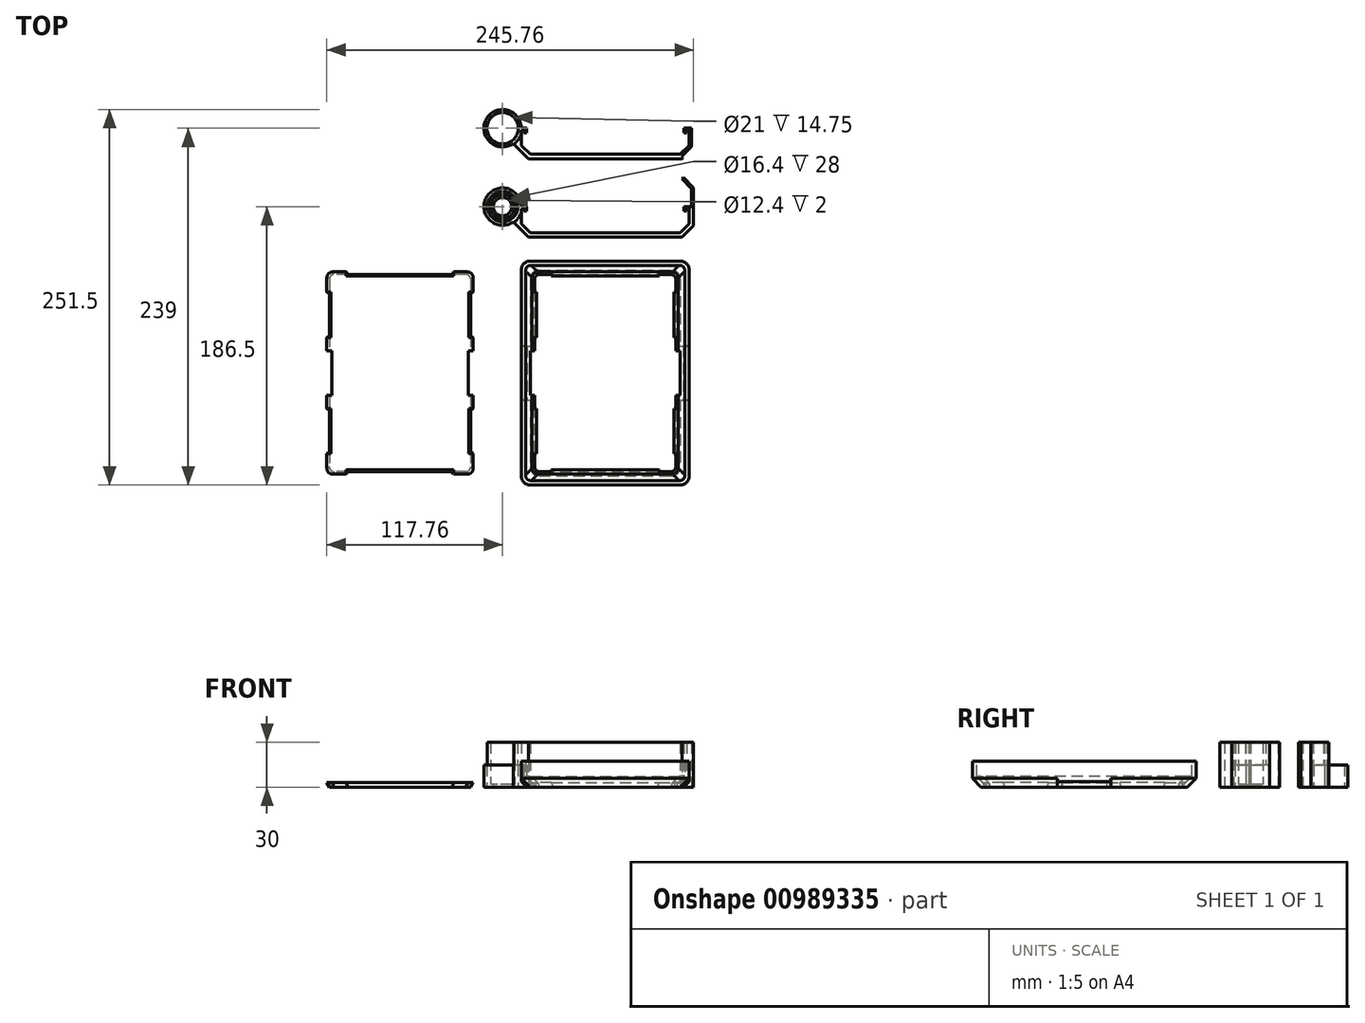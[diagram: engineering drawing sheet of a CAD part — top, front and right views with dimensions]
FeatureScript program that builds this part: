
annotation { "Feature Type Name" : "Feature", "Feature Type Description" : "" }
export const myFeature = defineFeature(function(context is Context, id is Id, definition is map)
    precondition{}
    {
        {
            assignVariable(context, id + "F0", {"name" : "hingeWidth", "anyValue" : 30});
        }
        {
            assignVariable(context, id + "F1", {"name" : "thickness", "anyValue" : 3});
        }
        {
            assignVariable(context, id + "F2", {"name" : "depth", "anyValue" : 17.5});
        }
        {
            var Q0;
            Q0=qCreatedBy(makeId("Top.planeOp"),FACE);
            var sketch = newSketch(context, id + "F3", { "sketchPlane" : qUnion([Q0])});
            skArc(sketch, "E0", {"start": v(12.5, 0) * mm, "mid": v(-11.06, 5.83) * mm, "end": v(7.07, -10.31) * mm});
            skLineSegment(sketch, "E1", {"start": v(0, 0) * mm, "end": v(125, 0) * mm, "construction": true});
            skLineSegment(sketch, "E2", {"start": v(125, -1.25) * mm, "end": v(125, -11.5) * mm});
            skLineSegment(sketch, "E3", {"start": v(125, -11.5) * mm, "end": v(119, -17.5) * mm});
            skLineSegment(sketch, "E4", {"start": v(18.5, -17.5) * mm, "end": v(12.5, -11.5) * mm});
            skLineSegment(sketch, "E5.0", {"start": v(17.26, -20.5) * mm, "end": v(7.07, -10.31) * mm});
            skLineSegment(sketch, "E5.1", {"start": v(120.24, -20.5) * mm, "end": v(17.26, -20.5) * mm});
            skLineSegment(sketch, "E5.2", {"start": v(128, -12.74) * mm, "end": v(120.24, -20.5) * mm});
            skLineSegment(sketch, "E5.3", {"start": v(128, 12.74) * mm, "end": v(128, -12.74) * mm});
            skLineSegment(sketch, "E6", {"start": v(126.5, 12.12) * mm, "end": v(120.14, 18.49) * mm});
            skLineSegment(sketch, "E7", {"start": v(120.14, 18.49) * mm, "end": v(121.2, 19.55) * mm});
            skLineSegment(sketch, "E8", {"start": v(121.2, 19.55) * mm, "end": v(128, 12.74) * mm});
            skLineSegment(sketch, "E9", {"start": v(125, 0) * mm, "end": v(126.5, 0) * mm});
            skLineSegment(sketch, "E10", {"start": v(126.5, 0) * mm, "end": v(126.5, 12.12) * mm});
            skArc(sketch, "E11", {"start": v(7.07, -10.31) * mm, "mid": v(11.06, -5.83) * mm, "end": v(12.5, 0) * mm});
            skArc(sketch, "E12", {"start": v(7.43, -10.67) * mm, "mid": v(10.58, -7.56) * mm, "end": v(12.5, -3.57) * mm});
            skCircle(sketch, "E13", {"center": v(0, 52.5) * mm, "radius": 12.5 * mm});
            skLineSegment(sketch, "E14", {"start": v(7.07, 42.19) * mm, "end": v(17.26, 32) * mm});
            skLineSegment(sketch, "E15", {"start": v(17.26, 32) * mm, "end": v(120.24, 32) * mm});
            skLineSegment(sketch, "E16", {"start": v(120.24, 32) * mm, "end": v(120.84, 32.6) * mm});
            skLineSegment(sketch, "E17", {"start": v(128, 39.76) * mm, "end": v(128, 52.5) * mm, "construction": true});
            skLineSegment(sketch, "E18", {"start": v(128, 52.5) * mm, "end": v(126.5, 52.5) * mm, "construction": true});
            skLineSegment(sketch, "E19", {"start": v(125, 51.25) * mm, "end": v(125, 41) * mm});
            skLineSegment(sketch, "E20", {"start": v(125, 41) * mm, "end": v(119, 35) * mm});
            skLineSegment(sketch, "E21", {"start": v(18.5, 35) * mm, "end": v(12.5, 41) * mm});
            skLineSegment(sketch, "E22", {"start": v(12.5, 41) * mm, "end": v(12.5, 48.93) * mm});
            skArc(sketch, "E23", {"start": v(7.43, 41.83) * mm, "mid": v(10.58, 44.94) * mm, "end": v(12.5, 48.93) * mm});
            skLineSegment(sketch, "E24", {"start": v(126.5, 52.5) * mm, "end": v(126.5, 40.38) * mm});
            skLineSegment(sketch, "E25", {"start": v(126.5, 40.38) * mm, "end": v(119.78, 33.66) * mm});
            skLineSegment(sketch, "E26", {"start": v(119.78, 33.66) * mm, "end": v(120.84, 32.6) * mm});
            skLineSegment(sketch, "E27", {"start": v(120.84, 32.6) * mm, "end": v(128, 39.76) * mm, "construction": true});
            skCircle(sketch, "E28", {"center": v(0, 0) * mm, "radius": 8.2 * mm});
            skCircle(sketch, "E29", {"center": v(0, 52.5) * mm, "radius": 10.5 * mm});
            skCircle(sketch, "E30", {"center": v(0, 0) * mm, "radius": 10.2 * mm});
            skLineSegment(sketch, "E31", {"start": v(12.5, -3.57) * mm, "end": v(12.5, -1.25) * mm});
            skLineSegment(sketch, "E32", {"start": v(125, 52.5) * mm, "end": v(126.5, 52.5) * mm});
            skLineSegment(sketch, "E33", {"start": v(12.5, 52.5) * mm, "end": v(125, 52.5) * mm, "construction": true});
            skCircle(sketch, "E34", {"center": v(0, 0) * mm, "radius": 6.2 * mm});
            skLineSegment(sketch, "E35", {"start": v(12.5, -3.57) * mm, "end": v(12.5, -11.5) * mm});
            skLineSegment(sketch, "E36", {"start": v(125, 52.5) * mm, "end": v(121.5, 52.5) * mm});
            skLineSegment(sketch, "E37", {"start": v(121.5, 52.5) * mm, "end": v(121.5, 49.5) * mm});
            skLineSegment(sketch, "E38", {"start": v(121.5, 49.5) * mm, "end": v(123.25, 49.5) * mm});
            skLineSegment(sketch, "E39", {"start": v(123.25, 49.5) * mm, "end": v(123.25, 51.25) * mm});
            skLineSegment(sketch, "E40", {"start": v(123.25, 51.25) * mm, "end": v(125, 51.25) * mm});
            skLineSegment(sketch, "E41", {"start": v(12.5, 52.5) * mm, "end": v(16, 52.5) * mm});
            skLineSegment(sketch, "E42", {"start": v(16, 52.5) * mm, "end": v(16, 49.5) * mm});
            skLineSegment(sketch, "E43", {"start": v(16, 49.5) * mm, "end": v(14.25, 49.5) * mm});
            skLineSegment(sketch, "E44", {"start": v(14.25, 49.5) * mm, "end": v(14.25, 51.25) * mm});
            skLineSegment(sketch, "E45", {"start": v(14.25, 51.25) * mm, "end": v(12.5, 51.25) * mm});
            skLineSegment(sketch, "E46", {"start": v(125, 0) * mm, "end": v(121.5, 0) * mm});
            skLineSegment(sketch, "E47", {"start": v(121.5, 0) * mm, "end": v(121.5, -3) * mm});
            skLineSegment(sketch, "E48", {"start": v(121.5, -3) * mm, "end": v(123.25, -3) * mm});
            skLineSegment(sketch, "E49", {"start": v(123.25, -3) * mm, "end": v(123.25, -1.25) * mm});
            skLineSegment(sketch, "E50", {"start": v(123.25, -1.25) * mm, "end": v(125, -1.25) * mm});
            skLineSegment(sketch, "E51", {"start": v(12.5, 0) * mm, "end": v(16, 0) * mm});
            skLineSegment(sketch, "E52", {"start": v(16, 0) * mm, "end": v(16, -3) * mm});
            skLineSegment(sketch, "E53", {"start": v(16, -3) * mm, "end": v(14.25, -3) * mm});
            skLineSegment(sketch, "E54", {"start": v(14.25, -3) * mm, "end": v(14.25, -1.25) * mm});
            skLineSegment(sketch, "E55", {"start": v(14.25, -1.25) * mm, "end": v(12.5, -1.25) * mm});
            skPoint(sketch, "E55.endSnap0", {"position": v(12.5, -1.79) * mm});
            skLineSegment(sketch, "E56", {"start": v(18.5, 35) * mm, "end": v(119, 35) * mm});
            skLineSegment(sketch, "E57", {"start": v(18.5, -17.5) * mm, "end": v(119, -17.5) * mm});
            skLineSegment(sketch, "E58", {"start": v(12.5, 48.93) * mm, "end": v(12.5, 51.25) * mm});
            skSolve(sketch);
        }
        {
            var Q0;
            {var subQ3=sQuery(id+"F3.wireOp",EDGE,"E15");Q0=makeQuery(id+"F3.imprint","IMPRINT",FACE,{"disambiguationData":[TD([[makeQuery(id+"F3.imprint","IMPRINT",EDGE,{"derivedFrom":subQ3}),1.0]])]});}
            var Q1;
            Q1=makeQuery(id+"F3.imprint","IMPRINT",FACE,{"disambiguationData":[TD([[makeQuery(id+"F3.imprint","IMPRINT",EDGE,{"derivedFrom":sQuery(id+"F3.wireOp",EDGE,"E2")}),1.0]])]});
            var Q2;
            Q2=makeQuery(id+"F3.imprint","IMPRINT",FACE,{"disambiguationData":[TD([[makeQuery(id+"F3.imprint","IMPRINT",EDGE,{"derivedFrom":sQuery(id+"F3.wireOp",EDGE,"E28")}),-1.0]])]});
            extrude(context, id + "F4", {"entities" : qUnion([Q0, Q1, Q2]), "depth" : (getVariable(context, 'hingeWidth')) * mm, "offsetDistance" : 25 * mm});
        }
        {
            var Q0;
            Q0=makeQuery(id+"F3.imprint","IMPRINT",FACE,{"disambiguationData":[TD([[makeQuery(id+"F3.imprint","IMPRINT",EDGE,{"derivedFrom":sQuery(id+"F3.wireOp",EDGE,"E29")}),-1.0]])]});
            var Q1;
            {var subQ5=sQuery(id+"F3.wireOp",EDGE,"E23");Q1=makeQuery(id+"F3.imprint","IMPRINT",FACE,{"disambiguationData":[TD([[makeQuery(id+"F3.imprint","IMPRINT",EDGE,{"derivedFrom":subQ5}),1.0]])]});}
            var Q2;
            Q2=makeQuery(id+"F3.imprint","IMPRINT",FACE,{"disambiguationData":[TD([[makeQuery(id+"F3.imprint","IMPRINT",EDGE,{"derivedFrom":sQuery(id+"F3.wireOp",EDGE,"E0")}),1.0]])]});
            var Q3;
            Q3=makeQuery(id+"F3.imprint","IMPRINT",FACE,{"disambiguationData":[TD([[makeQuery(id+"F3.imprint","IMPRINT",EDGE,{"derivedFrom":sQuery(id+"F3.wireOp",EDGE,"E28")}),-1.0]])]});
            var Q4;
            {var subQ0=sQuery(id+"F3.wireOp",EDGE,"E11");Q4=makeQuery(id+"F3.imprint","IMPRINT",FACE,{"disambiguationData":[TD([[makeQuery(id+"F3.imprint","IMPRINT",EDGE,{"derivedFrom":subQ0}),-1.0]])]});}
            extrude(context, id + "F5", {"entities" : qUnion([Q0, Q1, Q2, Q3, Q4]), "operationType" : NewBodyOperationType.ADD, "depth" : ((getVariable(context, 'hingeWidth') / 2) - .25) * mm, "offsetDistance" : 25 * mm});
        }
        {
            var Q0;
            Q0=makeQuery(id+"F3.imprint","IMPRINT",FACE,{"disambiguationData":[TD([[makeQuery(id+"F3.imprint","IMPRINT",EDGE,{"derivedFrom":sQuery(id+"F3.wireOp",EDGE,"E28")}),1.0]])]});
            extrude(context, id + "F6", {"entities" : qUnion([Q0]), "operationType" : NewBodyOperationType.ADD, "depth" : 2 * mm, "offsetDistance" : 25 * mm});
        }
        {
            var Q0;
            Q0=qCreatedBy(makeId("Top.planeOp"),FACE);
            var sketch = newSketch(context, id + "F7", { "sketchPlane" : qUnion([Q0])});
            skLineSegment(sketch, "E59.0", {"start": v(18.5, -17.5) * mm, "end": v(12.5, -11.5) * mm, "construction": true});
            skLineSegment(sketch, "E60.0", {"start": v(119, -17.5) * mm, "end": v(18.5, -17.5) * mm, "construction": true});
            skLineSegment(sketch, "E61.0", {"start": v(125, -11.5) * mm, "end": v(119, -17.5) * mm, "construction": true});
            skLineSegment(sketch, "E62", {"start": v(12.5, -11.5) * mm, "end": v(12.5, -36.5) * mm, "construction": true});
            skLineSegment(sketch, "E63", {"start": v(12.5, -36.5) * mm, "end": v(18.5, -36.5) * mm, "construction": true});
            skLineSegment(sketch, "E64", {"start": v(18.5, -36.5) * mm, "end": v(119, -36.5) * mm, "construction": true});
            skLineSegment(sketch, "E65", {"start": v(119, -36.5) * mm, "end": v(125, -36.5) * mm, "construction": true});
            skLineSegment(sketch, "E66", {"start": v(125, -36.5) * mm, "end": v(125, -42.5) * mm, "construction": true});
            skLineSegment(sketch, "E67", {"start": v(12.5, -36.5) * mm, "end": v(12.5, -42.5) * mm, "construction": true});
            skLineSegment(sketch, "E68", {"start": v(12.5, -42.5) * mm, "end": v(12.5, -180.5) * mm, "construction": true});
            skLineSegment(sketch, "E69", {"start": v(12.5, -180.5) * mm, "end": v(12.5, -186.5) * mm, "construction": true});
            skLineSegment(sketch, "E70", {"start": v(12.5, -186.5) * mm, "end": v(18.5, -186.5) * mm, "construction": true});
            skLineSegment(sketch, "E71", {"start": v(18.5, -186.5) * mm, "end": v(119, -186.5) * mm, "construction": true});
            skLineSegment(sketch, "E72", {"start": v(119, -186.5) * mm, "end": v(125, -186.5) * mm, "construction": true});
            skLineSegment(sketch, "E73", {"start": v(125, -186.5) * mm, "end": v(125, -180.5) * mm, "construction": true});
            skLineSegment(sketch, "E74", {"start": v(125, -180.5) * mm, "end": v(125, -42.5) * mm, "construction": true});
            skLineSegment(sketch, "E75.bottom", {"start": v(24.5, -42.5) * mm, "end": v(113, -42.5) * mm});
            skLineSegment(sketch, "E75.top", {"start": v(24.5, -180.5) * mm, "end": v(113, -180.5) * mm});
            skLineSegment(sketch, "E75.left", {"start": v(18.5, -48.5) * mm, "end": v(18.5, -174.5) * mm});
            skLineSegment(sketch, "E75.right", {"start": v(119, -48.5) * mm, "end": v(119, -174.5) * mm});
            skPoint(sketch, "E76.visualSharp", {"position": v(18.5, -42.5) * mm});
            skArc(sketch, "E76.filletArc", {"start": v(24.5, -42.5) * mm, "mid": v(20.26, -44.26) * mm, "end": v(18.5, -48.5) * mm});
            skPoint(sketch, "E77.visualSharp", {"position": v(119, -42.5) * mm});
            skArc(sketch, "E77.filletArc", {"start": v(119, -48.5) * mm, "mid": v(117.24, -44.26) * mm, "end": v(113, -42.5) * mm});
            skPoint(sketch, "E78.visualSharp", {"position": v(119, -180.5) * mm});
            skArc(sketch, "E78.filletArc", {"start": v(113, -180.5) * mm, "mid": v(117.24, -178.74) * mm, "end": v(119, -174.5) * mm});
            skPoint(sketch, "E79.visualSharp", {"position": v(18.5, -180.5) * mm});
            skArc(sketch, "E79.filletArc", {"start": v(18.5, -174.5) * mm, "mid": v(20.26, -178.74) * mm, "end": v(24.5, -180.5) * mm});
            skLineSegment(sketch, "E80", {"start": v(0, 0) * mm, "end": v(0, -36.5) * mm, "construction": true});
            skArc(sketch, "E81.0", {"start": v(24.5, -45.5) * mm, "mid": v(22.38, -46.38) * mm, "end": v(21.5, -48.5) * mm, "construction": true});
            skLineSegment(sketch, "E81.1", {"start": v(21.5, -48.5) * mm, "end": v(21.5, -174.5) * mm, "construction": true});
            skLineSegment(sketch, "E81.2", {"start": v(24.5, -45.5) * mm, "end": v(113, -45.5) * mm, "construction": true});
            skArc(sketch, "E81.3", {"start": v(21.5, -174.5) * mm, "mid": v(22.38, -176.62) * mm, "end": v(24.5, -177.5) * mm, "construction": true});
            skArc(sketch, "E81.4", {"start": v(116, -48.5) * mm, "mid": v(115.12, -46.38) * mm, "end": v(113, -45.5) * mm, "construction": true});
            skLineSegment(sketch, "E81.5", {"start": v(116, -48.5) * mm, "end": v(116, -174.5) * mm, "construction": true});
            skArc(sketch, "E81.6", {"start": v(113, -177.5) * mm, "mid": v(115.12, -176.62) * mm, "end": v(116, -174.5) * mm, "construction": true});
            skLineSegment(sketch, "E81.7", {"start": v(24.5, -177.5) * mm, "end": v(113, -177.5) * mm, "construction": true});
            skLineSegment(sketch, "E82.MirrorCS", {"start": v(-21.5, -48.5) * mm, "end": v(-21.5, -174.5) * mm});
            skArc(sketch, "E83.MirrorCS", {"start": v(-24.5, -45.5) * mm, "mid": v(-22.38, -46.38) * mm, "end": v(-21.5, -48.5) * mm});
            skLineSegment(sketch, "E84.MirrorCS", {"start": v(-24.5, -45.5) * mm, "end": v(-113, -45.5) * mm});
            skArc(sketch, "E85.MirrorCS", {"start": v(-116, -48.5) * mm, "mid": v(-115.12, -46.38) * mm, "end": v(-113, -45.5) * mm});
            skLineSegment(sketch, "E86.MirrorCS", {"start": v(-116, -48.5) * mm, "end": v(-116, -174.5) * mm});
            skArc(sketch, "E87.MirrorCS", {"start": v(-113, -177.5) * mm, "mid": v(-115.12, -176.62) * mm, "end": v(-116, -174.5) * mm});
            skLineSegment(sketch, "E88.MirrorCS", {"start": v(-24.5, -177.5) * mm, "end": v(-113, -177.5) * mm});
            skArc(sketch, "E89.MirrorCS", {"start": v(-21.5, -174.5) * mm, "mid": v(-22.38, -176.62) * mm, "end": v(-24.5, -177.5) * mm});
            skLineSegment(sketch, "E90", {"start": v(0, -36.5) * mm, "end": v(0, -186.5) * mm, "construction": true});
            skLineSegment(sketch, "E91", {"start": v(0, -111.5) * mm, "end": v(12.5, -111.5) * mm, "construction": true});
            skLineSegment(sketch, "E92", {"start": v(0, -96.5) * mm, "end": v(12.5, -96.5) * mm, "construction": true});
            skLineSegment(sketch, "E93", {"start": v(0, -126.5) * mm, "end": v(12.5, -126.5) * mm, "construction": true});
            skSolve(sketch);
        }
        {
            var Q0;
            Q0=qCreatedBy(makeId("Top.planeOp"),FACE);
            cPlane(context, id + "F8", {"entities" : qUnion([Q0]), "cplaneType" : CPlaneType.OFFSET, "offset" : (getVariable(context, 'thickness') * 2) * mm, "width" : 150 * mm, "height" : 150 * mm});
        }
        {
            var Q0;
            Q0=qCreatedBy(id+"F8.planeOp",FACE);
            var sketch = newSketch(context, id + "F9", { "sketchPlane" : qUnion([Q0])});
            skPoint(sketch, "E94.0", {"position": v(12.5, -36.5) * mm});
            skPoint(sketch, "E95.0", {"position": v(125, -186.5) * mm});
            skLineSegment(sketch, "E96.bottom", {"start": v(18.5, -36.5) * mm, "end": v(119, -36.5) * mm});
            skLineSegment(sketch, "E96.top", {"start": v(18.5, -186.5) * mm, "end": v(119, -186.5) * mm});
            skLineSegment(sketch, "E96.left", {"start": v(12.5, -42.5) * mm, "end": v(12.5, -180.5) * mm});
            skLineSegment(sketch, "E96.right", {"start": v(125, -42.5) * mm, "end": v(125, -180.5) * mm});
            skArc(sketch, "E97.filletArc", {"start": v(18.5, -36.5) * mm, "mid": v(14.26, -38.26) * mm, "end": v(12.5, -42.5) * mm});
            skPoint(sketch, "E98.visualSharp", {"position": v(125, -36.5) * mm});
            skArc(sketch, "E98.filletArc", {"start": v(125, -42.5) * mm, "mid": v(123.24, -38.26) * mm, "end": v(119, -36.5) * mm});
            skArc(sketch, "E99.filletArc", {"start": v(119, -186.5) * mm, "mid": v(123.24, -184.74) * mm, "end": v(125, -180.5) * mm});
            skPoint(sketch, "E100.visualSharp", {"position": v(12.5, -186.5) * mm});
            skArc(sketch, "E100.filletArc", {"start": v(12.5, -180.5) * mm, "mid": v(14.26, -184.74) * mm, "end": v(18.5, -186.5) * mm});
            skSolve(sketch);
        }
        {
            var Q0;
            Q0 = qSketchRegion(id + "F9", true);
            var Q1;
            Q1=makeQuery(id+"F7.imprint","IMPRINT",FACE,{"disambiguationData":[TD([[makeQuery(id+"F7.imprint","IMPRINT",EDGE,{"derivedFrom":sQuery(id+"F7.wireOp",EDGE,"E75.bottom")}),-1.0]])]});
            loft(context, id + "F10", {"sheetProfilesArray" : [{ "sheetProfileEntities" : qUnion([Q0]) }, { "sheetProfileEntities" : qUnion([Q1]) }]});
        }
        {
            var Q0;
            Q0 = qSketchRegion(id + "F9", true);
            extrude(context, id + "F11", {"entities" : qUnion([Q0]), "operationType" : NewBodyOperationType.ADD, "depth" : (getVariable(context, 'depth') - (getVariable(context, 'thickness') * 2)) * mm, "offsetDistance" : 25 * mm});
        }
        {
            var Q0;
            Q0=makeQuery(id+"F11.opExtrude","CAP_FACE",FACE,{"disambiguationData":[OSD([sQuery(id+"F9.wireOp",EDGE,"E96.bottom"),sQuery(id+"F9.wireOp",EDGE,"E96.top"),sQuery(id+"F9.wireOp",EDGE,"E96.left"),sQuery(id+"F9.wireOp",EDGE,"E96.right"),sQuery(id+"F9.wireOp",EDGE,"E97.filletArc"),sQuery(id+"F9.wireOp",EDGE,"E98.filletArc"),sQuery(id+"F9.wireOp",EDGE,"E99.filletArc"),sQuery(id+"F9.wireOp",EDGE,"E100.filletArc")])],"isStart":false});
            shell(context, id + "F12", {"entities" : qUnion([Q0]), "thickness" : (getVariable(context, 'thickness')) * mm});
        }
        {
            var Q0;
            Q0=makeQuery(id+"F12.opShell","OFFSET_FACE",FACE,{"disambiguationData":[OSD([makeQuery(id+"F7.imprint","IMPRINT",FACE,{"disambiguationData":[TD([[makeQuery(id+"F7.imprint","IMPRINT",EDGE,{"derivedFrom":sQuery(id+"F7.wireOp",EDGE,"E75.bottom")}),-1.0]])]})])]});
            var sketch = newSketch(context, id + "F13", { "sketchPlane" : qUnion([Q0])});
            skFitSpline(sketch, "E101.0.0", {"points": [v(19.74, -175.38) * mm, v(19.74, -175.5) * mm, v(19.76, -175.76) * mm, v(19.83, -176.13) * mm, v(19.93, -176.5) * mm, v(20.07, -176.84) * mm, v(20.24, -177.17) * mm, v(20.51, -177.6) * mm, v(20.83, -177.99) * mm, v(21.2, -178.33) * mm, v(21.6, -178.63) * mm, v(22.04, -178.88) * mm, v(22.51, -179.07) * mm, v(23, -179.2) * mm, v(23.37, -179.26) * mm, v(23.62, -179.26) * mm], "construction": true});
            skLineSegment(sketch, "E101.0.1", {"start": v(113.88, -179.26) * mm, "end": v(23.62, -179.26) * mm, "construction": true});
            skFitSpline(sketch, "E101.0.2", {"points": [v(113.88, -179.26) * mm, v(114, -179.26) * mm, v(114.26, -179.24) * mm, v(114.63, -179.17) * mm, v(115, -179.07) * mm, v(115.34, -178.93) * mm, v(115.67, -178.76) * mm, v(116.1, -178.49) * mm, v(116.49, -178.17) * mm, v(116.83, -177.8) * mm, v(117.13, -177.4) * mm, v(117.38, -176.96) * mm, v(117.57, -176.49) * mm, v(117.7, -176) * mm, v(117.76, -175.63) * mm, v(117.76, -175.38) * mm], "construction": true});
            skLineSegment(sketch, "E101.0.3", {"start": v(117.76, -175.38) * mm, "end": v(117.76, -47.62) * mm, "construction": true});
            skFitSpline(sketch, "E101.0.4", {"points": [v(117.76, -47.62) * mm, v(117.76, -47.5) * mm, v(117.74, -47.24) * mm, v(117.67, -46.87) * mm, v(117.57, -46.5) * mm, v(117.43, -46.16) * mm, v(117.26, -45.83) * mm, v(116.99, -45.4) * mm, v(116.67, -45.01) * mm, v(116.3, -44.67) * mm, v(115.9, -44.37) * mm, v(115.46, -44.12) * mm, v(114.99, -43.93) * mm, v(114.5, -43.8) * mm, v(114.13, -43.74) * mm, v(113.88, -43.74) * mm], "construction": true});
            skLineSegment(sketch, "E101.0.5", {"start": v(113.88, -43.74) * mm, "end": v(23.62, -43.74) * mm, "construction": true});
            skFitSpline(sketch, "E101.0.6", {"points": [v(23.62, -43.74) * mm, v(23.5, -43.74) * mm, v(23.24, -43.76) * mm, v(22.87, -43.83) * mm, v(22.5, -43.93) * mm, v(22.16, -44.07) * mm, v(21.83, -44.24) * mm, v(21.4, -44.51) * mm, v(21.01, -44.83) * mm, v(20.67, -45.2) * mm, v(20.37, -45.6) * mm, v(20.12, -46.04) * mm, v(19.93, -46.51) * mm, v(19.8, -47) * mm, v(19.74, -47.37) * mm, v(19.74, -47.62) * mm], "construction": true});
            skLineSegment(sketch, "E101.0.7", {"start": v(19.74, -175.38) * mm, "end": v(19.74, -47.62) * mm, "construction": true});
            skLineSegment(sketch, "E102.0", {"start": v(0, 0) * mm, "end": v(0, -36.5) * mm, "construction": true});
            skLineSegment(sketch, "E103.MirrorCS", {"start": v(-113.88, -43.74) * mm, "end": v(-23.62, -43.74) * mm});
            skLineSegment(sketch, "E104.MirrorCS", {"start": v(-19.74, -175.38) * mm, "end": v(-19.74, -47.62) * mm});
            skLineSegment(sketch, "E105.MirrorCS", {"start": v(-113.88, -179.26) * mm, "end": v(-23.62, -179.26) * mm});
            skLineSegment(sketch, "E106.MirrorCS", {"start": v(-117.76, -175.38) * mm, "end": v(-117.76, -47.62) * mm});
            skArc(sketch, "E107", {"start": v(-113.88, -43.74) * mm, "mid": v(-116.62, -44.88) * mm, "end": v(-117.76, -47.62) * mm});
            skArc(sketch, "E108", {"start": v(-19.74, -47.62) * mm, "mid": v(-20.88, -44.88) * mm, "end": v(-23.62, -43.74) * mm});
            skArc(sketch, "E109", {"start": v(-23.62, -179.26) * mm, "mid": v(-20.88, -178.12) * mm, "end": v(-19.74, -175.38) * mm});
            skArc(sketch, "E110", {"start": v(-117.76, -175.38) * mm, "mid": v(-116.62, -178.12) * mm, "end": v(-113.88, -179.26) * mm});
            skSolve(sketch);
        }
        {
            var Q0;
            Q0=makeQuery(id+"F7.imprint","IMPRINT",FACE,{"disambiguationData":[TD([[makeQuery(id+"F7.imprint","IMPRINT",EDGE,{"derivedFrom":sQuery(id+"F7.wireOp",EDGE,"E82.MirrorCS")}),-1.0]])]});
            var Q1;
            Q1=makeQuery(id+"F13.imprint","IMPRINT",FACE,{"disambiguationData":[TD([[makeQuery(id+"F13.imprint","IMPRINT",EDGE,{"derivedFrom":sQuery(id+"F13.wireOp",EDGE,"E103.MirrorCS")}),-1.0]])]});
            loft(context, id + "F14", {"sheetProfilesArray" : [{ "sheetProfileEntities" : qUnion([Q0]) }, { "sheetProfileEntities" : qUnion([Q1]) }]});
        }
        {
            var Q0;
            Q0=qCreatedBy(makeId("Top.planeOp"),FACE);
            var sketch = newSketch(context, id + "F15", { "sketchPlane" : qUnion([Q0])});
            skLineSegment(sketch, "E111.0", {"start": v(-24.5, -45.5) * mm, "end": v(-113, -45.5) * mm, "construction": true});
            skLineSegment(sketch, "E112.0", {"start": v(-116, -48.5) * mm, "end": v(-116, -174.5) * mm, "construction": true});
            skLineSegment(sketch, "E113.0", {"start": v(-21.5, -48.5) * mm, "end": v(-21.5, -174.5) * mm, "construction": true});
            skLineSegment(sketch, "E114.0", {"start": v(-24.5, -177.5) * mm, "end": v(-113, -177.5) * mm, "construction": true});
            skLineSegment(sketch, "E115.0", {"start": v(-23.62, -43.74) * mm, "end": v(-113.88, -43.74) * mm, "construction": true});
            skLineSegment(sketch, "E116.0", {"start": v(-113.88, -179.26) * mm, "end": v(-23.62, -179.26) * mm, "construction": true});
            skLineSegment(sketch, "E117.0", {"start": v(-19.74, -175.38) * mm, "end": v(-19.74, -47.62) * mm, "construction": true});
            skLineSegment(sketch, "E118.0", {"start": v(-117.76, -47.62) * mm, "end": v(-117.76, -175.38) * mm, "construction": true});
            skLineSegment(sketch, "E119.bottom", {"start": v(-103.75, -43.74) * mm, "end": v(-33.75, -43.74) * mm});
            skLineSegment(sketch, "E119.top", {"start": v(-103.75, -45.5) * mm, "end": v(-33.75, -45.5) * mm});
            skLineSegment(sketch, "E119.left", {"start": v(-103.75, -43.74) * mm, "end": v(-103.75, -45.5) * mm});
            skLineSegment(sketch, "E119.right", {"start": v(-33.75, -43.74) * mm, "end": v(-33.75, -45.5) * mm});
            skLineSegment(sketch, "E120", {"start": v(-68.75, -43.74) * mm, "end": v(-68.75, -45.5) * mm, "construction": true});
            skLineSegment(sketch, "E121.bottom", {"start": v(-103.75, -177.5) * mm, "end": v(-33.75, -177.5) * mm});
            skLineSegment(sketch, "E121.top", {"start": v(-103.75, -179.26) * mm, "end": v(-33.75, -179.26) * mm});
            skLineSegment(sketch, "E121.left", {"start": v(-103.75, -177.5) * mm, "end": v(-103.75, -179.26) * mm});
            skLineSegment(sketch, "E121.right", {"start": v(-33.75, -177.5) * mm, "end": v(-33.75, -179.26) * mm});
            skLineSegment(sketch, "E122.0", {"start": v(0, -126.5) * mm, "end": v(12.5, -126.5) * mm, "construction": true});
            skLineSegment(sketch, "E123.0", {"start": v(0, -111.5) * mm, "end": v(12.5, -111.5) * mm, "construction": true});
            skLineSegment(sketch, "E124.0", {"start": v(0, -96.5) * mm, "end": v(12.5, -96.5) * mm, "construction": true});
            skLineSegment(sketch, "E125.bottom", {"start": v(-19.74, -126.5) * mm, "end": v(-23, -126.5) * mm});
            skLineSegment(sketch, "E125.top", {"start": v(-19.74, -96.5) * mm, "end": v(-23, -96.5) * mm});
            skLineSegment(sketch, "E125.left", {"start": v(-19.74, -126.5) * mm, "end": v(-19.74, -96.5) * mm});
            skLineSegment(sketch, "E125.right", {"start": v(-23, -126.5) * mm, "end": v(-23, -96.5) * mm});
            skLineSegment(sketch, "E126.bottom", {"start": v(-114.5, -96.5) * mm, "end": v(-117.76, -96.5) * mm});
            skLineSegment(sketch, "E126.top", {"start": v(-114.5, -126.5) * mm, "end": v(-117.76, -126.5) * mm});
            skLineSegment(sketch, "E126.left", {"start": v(-114.5, -96.5) * mm, "end": v(-114.5, -126.5) * mm});
            skLineSegment(sketch, "E126.right", {"start": v(-117.76, -96.5) * mm, "end": v(-117.76, -126.5) * mm});
            skLineSegment(sketch, "E127.bottom", {"start": v(-19.74, -86.5) * mm, "end": v(-21.5, -86.5) * mm});
            skLineSegment(sketch, "E127.top", {"start": v(-19.74, -58.5) * mm, "end": v(-21.5, -58.5) * mm});
            skLineSegment(sketch, "E127.left", {"start": v(-19.74, -86.5) * mm, "end": v(-19.74, -58.5) * mm});
            skLineSegment(sketch, "E127.right", {"start": v(-21.5, -86.5) * mm, "end": v(-21.5, -58.5) * mm});
            skLineSegment(sketch, "E128.bottom", {"start": v(-21.5, -136.5) * mm, "end": v(-19.74, -136.5) * mm});
            skLineSegment(sketch, "E128.top", {"start": v(-21.5, -164.5) * mm, "end": v(-19.74, -164.5) * mm});
            skLineSegment(sketch, "E128.left", {"start": v(-21.5, -136.5) * mm, "end": v(-21.5, -164.5) * mm});
            skLineSegment(sketch, "E128.right", {"start": v(-19.74, -136.5) * mm, "end": v(-19.74, -164.5) * mm});
            skLineSegment(sketch, "E129.bottom", {"start": v(-116, -58.5) * mm, "end": v(-117.76, -58.5) * mm});
            skLineSegment(sketch, "E129.top", {"start": v(-116, -86.5) * mm, "end": v(-117.76, -86.5) * mm});
            skLineSegment(sketch, "E129.left", {"start": v(-116, -58.5) * mm, "end": v(-116, -86.5) * mm});
            skLineSegment(sketch, "E129.right", {"start": v(-117.76, -58.5) * mm, "end": v(-117.76, -86.5) * mm});
            skLineSegment(sketch, "E130.bottom", {"start": v(-116, -136.5) * mm, "end": v(-117.76, -136.5) * mm});
            skLineSegment(sketch, "E130.top", {"start": v(-116, -164.5) * mm, "end": v(-117.76, -164.5) * mm});
            skLineSegment(sketch, "E130.left", {"start": v(-116, -136.5) * mm, "end": v(-116, -164.5) * mm});
            skLineSegment(sketch, "E130.right", {"start": v(-117.76, -136.5) * mm, "end": v(-117.76, -164.5) * mm});
            skLineSegment(sketch, "E131.0", {"start": v(21.5, -48.5) * mm, "end": v(21.5, -174.5) * mm, "construction": true});
            skLineSegment(sketch, "E132.0", {"start": v(116, -48.5) * mm, "end": v(116, -174.5) * mm, "construction": true});
            skLineSegment(sketch, "E133.bottom", {"start": v(21.5, -96.5) * mm, "end": v(18.5, -96.5) * mm});
            skLineSegment(sketch, "E133.top", {"start": v(21.5, -126.5) * mm, "end": v(18.5, -126.5) * mm});
            skLineSegment(sketch, "E133.left", {"start": v(21.5, -96.5) * mm, "end": v(21.5, -126.5) * mm});
            skLineSegment(sketch, "E134.0", {"start": v(18.5, -48.5) * mm, "end": v(18.5, -174.5) * mm, "construction": true});
            skLineSegment(sketch, "E135.bottom", {"start": v(116, -96.5) * mm, "end": v(119, -96.5) * mm});
            skLineSegment(sketch, "E135.top", {"start": v(116, -126.5) * mm, "end": v(119, -126.5) * mm});
            skLineSegment(sketch, "E135.left", {"start": v(116, -96.5) * mm, "end": v(116, -126.5) * mm});
            skLineSegment(sketch, "E135.right", {"start": v(119, -96.5) * mm, "end": v(119, -126.5) * mm});
            skLineSegment(sketch, "E136.bottom", {"start": v(119, -96.5) * mm, "end": v(119, -96.5) * mm});
            skLineSegment(sketch, "E136.top", {"start": v(119, -126.5) * mm, "end": v(119, -126.5) * mm});
            skLineSegment(sketch, "E137", {"start": v(18.5, -96.5) * mm, "end": v(18.5, -126.5) * mm});
            skSolve(sketch);
        }
        {
            var Q0;
            Q0=makeQuery(id+"F15.imprint","IMPRINT",FACE,{"disambiguationData":[TD([[makeQuery(id+"F15.imprint","IMPRINT",EDGE,{"derivedFrom":sQuery(id+"F15.wireOp",EDGE,"E119.bottom")}),-1.0]])]});
            var Q1;
            Q1=makeQuery(id+"F15.imprint","IMPRINT",FACE,{"disambiguationData":[TD([[makeQuery(id+"F15.imprint","IMPRINT",EDGE,{"derivedFrom":sQuery(id+"F15.wireOp",EDGE,"E121.bottom")}),-1.0]])]});
            var Q2;
            Q2=makeQuery(id+"F15.imprint","IMPRINT",FACE,{"disambiguationData":[TD([[makeQuery(id+"F15.imprint","IMPRINT",EDGE,{"derivedFrom":sQuery(id+"F15.wireOp",EDGE,"E129.bottom")}),1.0]])]});
            var Q3;
            Q3=makeQuery(id+"F15.imprint","IMPRINT",FACE,{"disambiguationData":[TD([[makeQuery(id+"F15.imprint","IMPRINT",EDGE,{"derivedFrom":sQuery(id+"F15.wireOp",EDGE,"E130.bottom")}),1.0]])]});
            var Q4;
            Q4=makeQuery(id+"F15.imprint","IMPRINT",FACE,{"disambiguationData":[TD([[makeQuery(id+"F15.imprint","IMPRINT",EDGE,{"derivedFrom":sQuery(id+"F15.wireOp",EDGE,"E127.bottom")}),-1.0]])]});
            var Q5;
            Q5=makeQuery(id+"F15.imprint","IMPRINT",FACE,{"disambiguationData":[TD([[makeQuery(id+"F15.imprint","IMPRINT",EDGE,{"derivedFrom":sQuery(id+"F15.wireOp",EDGE,"E128.bottom")}),-1.0]])]});
            extrude(context, id + "F16", {"entities" : qUnion([Q0, Q1, Q2, Q3, Q4, Q5]), "operationType" : NewBodyOperationType.REMOVE, "endBound" : BoundingType.THROUGH_ALL, "depth" : 25 * mm, "offsetDistance" : 25 * mm, "hasDraft" : true, "draftAngle" : 20 * degree});
        }
        {
            var Q0;
            Q0=sQuery(id+"F7.wireOp",EDGE,"E91");
            cPlane(context, id + "F17", {"entities" : qUnion([Q0]), "cplaneType" : CPlaneType.LINE_ANGLE, "offset" : 25 * mm, "angle" : 0 * degree, "width" : 150 * mm, "height" : 150 * mm});
        }
        {
            var Q0;
            Q0=makeQuery(id+"F14.opLoft","SWEPT_BODY",BODY,{"disambiguationData":[OSD([makeQuery(id+"F7.imprint","IMPRINT",FACE,{"disambiguationData":[TD([[makeQuery(id+"F7.imprint","IMPRINT",EDGE,{"derivedFrom":sQuery(id+"F7.wireOp",EDGE,"E82.MirrorCS")}),-1.0]])]}),makeQuery(id+"F13.imprint","IMPRINT",FACE,{"disambiguationData":[TD([[makeQuery(id+"F13.imprint","IMPRINT",EDGE,{"derivedFrom":sQuery(id+"F13.wireOp",EDGE,"E103.MirrorCS")}),-1.0]])]})])]});
            var Q1;
            Q1=qCreatedBy(makeId("Right.planeOp"),FACE);
            mirror(context, id + "F18", {"operationType" : NewBodyOperationType.REMOVE, "entities" : qUnion([Q0]), "mirrorPlane" : qUnion([Q1])});
        }
        {
            var Q0;
            Q0=makeQuery(id+"F15.imprint","IMPRINT",FACE,{"disambiguationData":[TD([[makeQuery(id+"F15.imprint","IMPRINT",EDGE,{"derivedFrom":sQuery(id+"F15.wireOp",EDGE,"E126.bottom")}),1.0]])]});
            var Q1;
            Q1=makeQuery(id+"F15.imprint","IMPRINT",FACE,{"disambiguationData":[TD([[makeQuery(id+"F15.imprint","IMPRINT",EDGE,{"derivedFrom":sQuery(id+"F15.wireOp",EDGE,"E125.bottom")}),-1.0]])]});
            var Q2;
            Q2=makeQuery(id+"F15.imprint","IMPRINT",FACE,{"disambiguationData":[TD([[makeQuery(id+"F15.imprint","IMPRINT",EDGE,{"derivedFrom":sQuery(id+"F15.wireOp",EDGE,"E133.bottom")}),1.0]])]});
            var Q3;
            Q3=makeQuery(id+"F15.imprint","IMPRINT",FACE,{"disambiguationData":[TD([[makeQuery(id+"F15.imprint","IMPRINT",EDGE,{"derivedFrom":sQuery(id+"F15.wireOp",EDGE,"E135.bottom")}),-1.0]])]});
            extrude(context, id + "F19", {"entities" : qUnion([Q0, Q1, Q2, Q3]), "operationType" : NewBodyOperationType.REMOVE, "endBound" : BoundingType.THROUGH_ALL, "depth" : 25 * mm, "offsetDistance" : 25 * mm});
        }
        {
            var Q0;
            Q0=qCreatedBy(id+"F17.planeOp",FACE);
            var sketch = newSketch(context, id + "F20", { "sketchPlane" : qUnion([Q0])});
            skFitSpline(sketch, "E138.0.0", {"points": [v(-19.74, 3) * mm, v(-18.33, 4.41) * mm, v(-16.91, 5.83) * mm, v(-15.5, 7.24) * mm], "construction": true});
            skFitSpline(sketch, "E138.0.2", {"points": [v(-15.5, 7.24) * mm, v(-16.91, 5.83) * mm, v(-18.33, 4.41) * mm, v(-19.74, 3) * mm], "construction": true});
            skFitSpline(sketch, "E139.0.1", {"points": [v(-15.5, 7.24) * mm, v(-15.5, 7.28) * mm, v(-15.5, 7.3) * mm, v(-15.5, 7.34) * mm], "construction": true});
            skLineSegment(sketch, "E139.0.2", {"start": v(-15.5, 7.34) * mm, "end": v(-15.5, 17.5) * mm, "construction": true});
            skLineSegment(sketch, "E139.0.4", {"start": v(-15.5, 17.5) * mm, "end": v(-15.5, 7.34) * mm, "construction": true});
            skFitSpline(sketch, "E139.0.5", {"points": [v(-15.5, 7.34) * mm, v(-15.5, 7.3) * mm, v(-15.5, 7.28) * mm, v(-15.5, 7.24) * mm], "construction": true});
            skLineSegment(sketch, "E140.0", {"start": v(-12.5, 17.5) * mm, "end": v(-12.5, 6) * mm, "construction": true});
            skFitSpline(sketch, "E141.0", {"points": [v(-12.5, 6) * mm, v(-14.5, 4) * mm, v(-16.5, 2) * mm, v(-18.5, 0) * mm], "construction": true});
            skLineSegment(sketch, "E142", {"start": v(-12.5, 6) * mm, "end": v(-16, 9.5) * mm, "construction": true});
            skLineSegment(sketch, "E143", {"start": v(-16, 9.5) * mm, "end": v(-16, 13) * mm, "construction": true});
            skLineSegment(sketch, "E144", {"start": v(-16, 13) * mm, "end": v(-12.5, 13) * mm, "construction": true});
            skFitSpline(sketch, "E145.0", {"points": [v(-125, 6) * mm, v(-123, 4) * mm, v(-121, 2) * mm, v(-119, 0) * mm], "construction": true});
            skLineSegment(sketch, "E146.0", {"start": v(-125, 17.5) * mm, "end": v(-125, 6) * mm, "construction": true});
            skLineSegment(sketch, "E147.bottom", {"start": v(-12.5, 13) * mm, "end": v(-125, 13) * mm});
            skLineSegment(sketch, "E147.top", {"start": v(-12.5, 0) * mm, "end": v(-125, 0) * mm});
            skLineSegment(sketch, "E147.left", {"start": v(-12.5, 13) * mm, "end": v(-12.5, 0) * mm});
            skLineSegment(sketch, "E147.right", {"start": v(-125, 13) * mm, "end": v(-125, 0) * mm});
            skLineSegment(sketch, "E148", {"start": v(-12.5, 6) * mm, "end": v(-18.5, 0) * mm});
            skLineSegment(sketch, "E149", {"start": v(-16.38, 0) * mm, "end": v(-12.5, 3.88) * mm});
            skLineSegment(sketch, "E150", {"start": v(-12.5, 3.88) * mm, "end": v(-12.5, 6) * mm});
            skLineSegment(sketch, "E151", {"start": v(-119, 0) * mm, "end": v(-125, 6) * mm});
            skLineSegment(sketch, "E152", {"start": v(-125, 6) * mm, "end": v(-125, 3.88) * mm});
            skLineSegment(sketch, "E153", {"start": v(-125, 3.88) * mm, "end": v(-121.12, 0) * mm});
            skLineSegment(sketch, "E154", {"start": v(-121.12, 0) * mm, "end": v(-119, 0) * mm});
            skLineSegment(sketch, "E155", {"start": v(-12.5, 3.88) * mm, "end": v(-11, 5.38) * mm});
            skLineSegment(sketch, "E156", {"start": v(-11, 5.38) * mm, "end": v(-11, 11.5) * mm});
            skLineSegment(sketch, "E157", {"start": v(-11, 11.5) * mm, "end": v(-12.5, 13) * mm});
            skLineSegment(sketch, "E158", {"start": v(-125, 3.88) * mm, "end": v(-126.5, 5.38) * mm});
            skLineSegment(sketch, "E159", {"start": v(-126.5, 5.38) * mm, "end": v(-126.5, 11.5) * mm});
            skLineSegment(sketch, "E160", {"start": v(-126.5, 11.5) * mm, "end": v(-125, 13) * mm});
            skLineSegment(sketch, "E161", {"start": v(-68.75, 13) * mm, "end": v(-68.75, 0) * mm});
            skSolve(sketch);
        }
        {
            var Q0;
            {var subQ0=sQuery(id+"F20.wireOp",EDGE,"E148");Q0=makeQuery(id+"F20.imprint","IMPRINT",FACE,{"disambiguationData":[TD([[makeQuery(id+"F20.imprint","IMPRINT",EDGE,{"derivedFrom":subQ0}),1.0]])]});}
            var Q1;
            Q1=makeQuery(id+"F20.imprint","IMPRINT",FACE,{"disambiguationData":[TD([[makeQuery(id+"F20.imprint","IMPRINT",EDGE,{"derivedFrom":sQuery(id+"F20.wireOp",EDGE,"E151")}),1.0]])]});
            var Q2;
            {var subQ2=sQuery(id+"F20.wireOp",EDGE,"E150");Q2=makeQuery(id+"F20.imprint","IMPRINT",FACE,{"disambiguationData":[TD([[makeQuery(id+"F20.imprint","IMPRINT",EDGE,{"derivedFrom":subQ2}),-1.0]])]});}
            var Q3;
            {var subQ0=sQuery(id+"F20.wireOp",EDGE,"E152");Q3=makeQuery(id+"F20.imprint","IMPRINT",FACE,{"disambiguationData":[TD([[makeQuery(id+"F20.imprint","IMPRINT",EDGE,{"derivedFrom":subQ0}),-1.0]])]});}
            extrude(context, id + "F21", {"entities" : qUnion([Q0, Q1, Q2, Q3]), "operationType" : NewBodyOperationType.ADD, "depth" : (getVariable(context, 'hingeWidth') + (getVariable(context, 'thickness') * 2)) * mm, "offsetDistance" : 25 * mm, "symmetric" : true});
        }
    });
